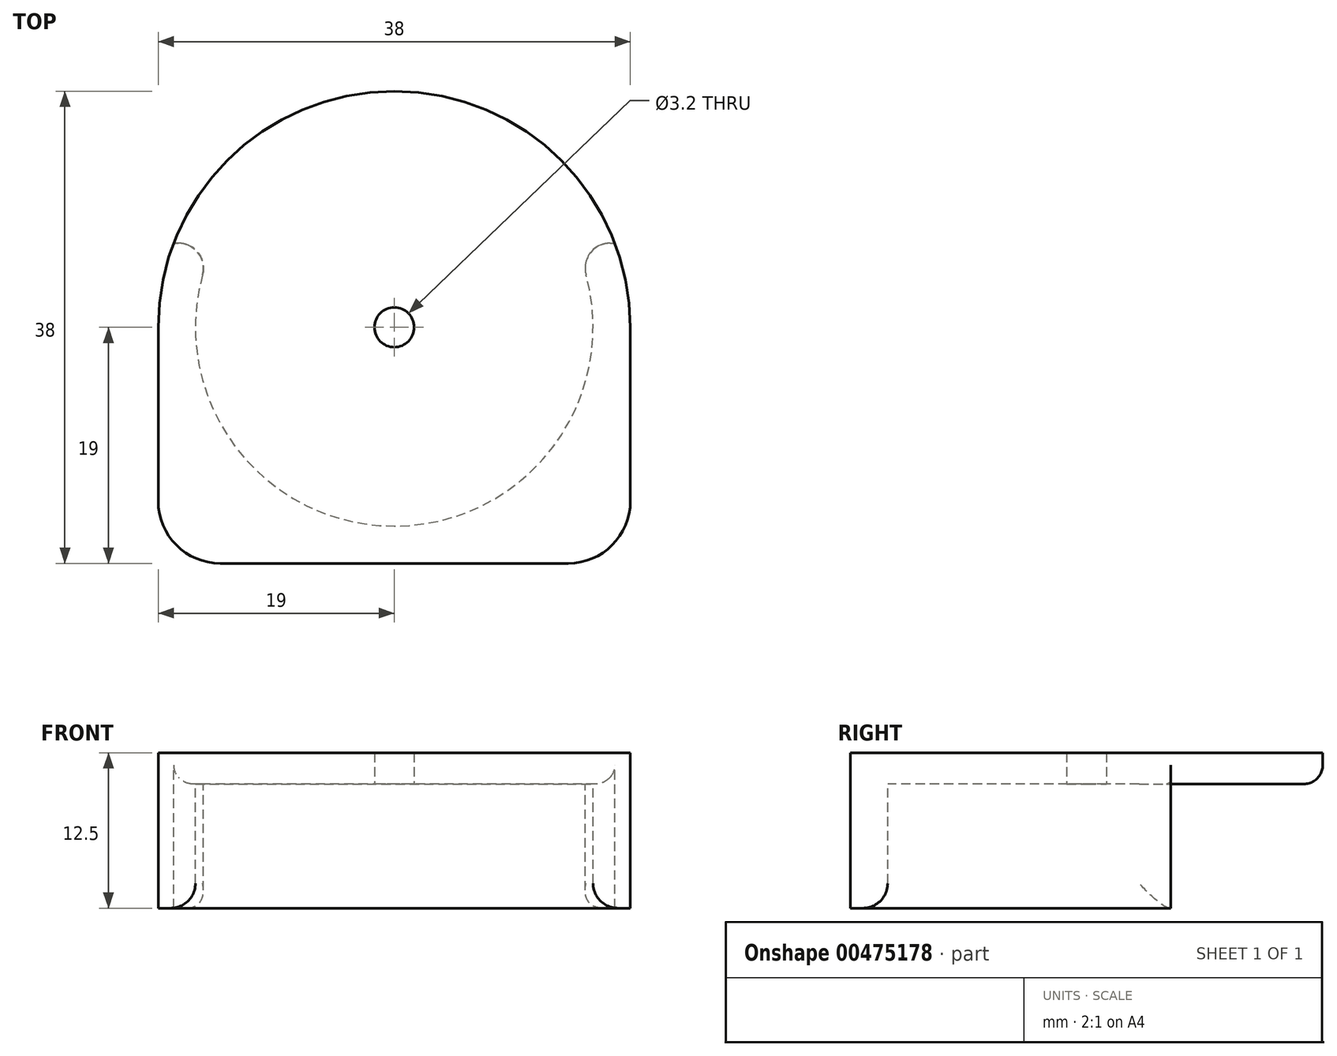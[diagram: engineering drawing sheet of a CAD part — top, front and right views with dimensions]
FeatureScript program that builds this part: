
annotation { "Feature Type Name" : "Feature", "Feature Type Description" : "" }
export const myFeature = defineFeature(function(context is Context, id is Id, definition is map)
    precondition{}
    {
        {
            var Q0;
            Q0=qCreatedBy(makeId("Top.planeOp"),FACE);
            var sketch = newSketch(context, id + "F0", { "sketchPlane" : qUnion([Q0])});
            skArc(sketch, "E0", {"start": v(-14.5, 6.76) * mm, "mid": v(0, -16) * mm, "end": v(14.5, 6.76) * mm});
            skCircle(sketch, "E1", {"center": v(0, 0) * mm, "radius": 19 * mm});
            skLineSegment(sketch, "E2", {"start": v(-14.5, 6.76) * mm, "end": v(14.5, 6.76) * mm});
            skLineSegment(sketch, "E3.bottom", {"start": v(14, -19) * mm, "end": v(-14, -19) * mm});
            skLineSegment(sketch, "E3.left", {"start": v(19, -14) * mm, "end": v(19, 0) * mm});
            skLineSegment(sketch, "E3.right", {"start": v(-19, -14) * mm, "end": v(-19, 0) * mm});
            skPoint(sketch, "E4.orphan", {"position": v(-19, 19) * mm});
            skPoint(sketch, "E5.orphan", {"position": v(19, 19) * mm});
            skPoint(sketch, "E6.visualSharp", {"position": v(-19, -19) * mm});
            skArc(sketch, "E6.filletArc", {"start": v(-19, -14) * mm, "mid": v(-17.54, -17.54) * mm, "end": v(-14, -19) * mm});
            skPoint(sketch, "E7.visualSharp", {"position": v(19, -19) * mm});
            skArc(sketch, "E7.filletArc", {"start": v(14, -19) * mm, "mid": v(17.54, -17.54) * mm, "end": v(19, -14) * mm});
            skLineSegment(sketch, "E8", {"start": v(-14.5, 6.76) * mm, "end": v(-17.76, 6.76) * mm});
            skLineSegment(sketch, "E9", {"start": v(14.5, 6.76) * mm, "end": v(17.76, 6.76) * mm});
            skSolve(sketch);
        }
        {
            var Q0;
            Q0 = qSketchRegion(id + "F0", true);
            var Q1;
            Q1=makeQuery(id+"F0.imprint","IMPRINT",FACE,{"disambiguationData":[TD([[makeQuery(id+"F0.imprint","IMPRINT",EDGE,{"derivedFrom":sQuery(id+"F0.wireOp",EDGE,"E0")}),1.0]])]});
            extrude(context, id + "F1", {"entities" : qUnion([Q0, Q1]), "depth" : 2.5 * mm, "offsetDistance" : 25 * mm});
        }
        {
            var Q0;
            Q0=makeQuery(id+"F0.imprint","IMPRINT",FACE,{"disambiguationData":[TD([[makeQuery(id+"F0.imprint","IMPRINT",EDGE,{"derivedFrom":sQuery(id+"F0.wireOp",EDGE,"E0")}),-1.0]])]});
            var Q1;
            {var subQ0=sQuery(id+"F0.wireOp",EDGE,"E3.left");Q1=makeQuery(id+"F0.imprint","IMPRINT",FACE,{"disambiguationData":[TD([[makeQuery(id+"F0.imprint","IMPRINT",EDGE,{"derivedFrom":subQ0}),1.0]])]});}
            var Q2;
            {var subQ0=sQuery(id+"F0.wireOp",EDGE,"E3.right");Q2=makeQuery(id+"F0.imprint","IMPRINT",FACE,{"disambiguationData":[TD([[makeQuery(id+"F0.imprint","IMPRINT",EDGE,{"derivedFrom":subQ0}),-1.0]])]});}
            extrude(context, id + "F2", {"entities" : qUnion([Q0, Q1, Q2]), "operationType" : NewBodyOperationType.ADD, "oppositeDirection" : true, "depth" : 10 * mm, "offsetDistance" : 25 * mm});
        }
        {
            var Q0;
            Q0=makeQuery(id+"F0.imprint","IMPRINT",FACE,{"disambiguationData":[TD([[makeQuery(id+"F0.imprint","IMPRINT",EDGE,{"derivedFrom":sQuery(id+"F0.wireOp",EDGE,"E0")}),1.0]])]});
            var sketch = newSketch(context, id + "F3", { "sketchPlane" : qUnion([Q0])});
            skCircle(sketch, "E10", {"center": v(0, 0) * mm, "radius": 1.6 * mm});
            skSolve(sketch);
        }
        {
            var Q0;
            Q0=makeQuery(id+"F3.imprint","IMPRINT",FACE,{"disambiguationData":[TD([[makeQuery(id+"F3.imprint","IMPRINT",EDGE,{"derivedFrom":sQuery(id+"F3.wireOp",EDGE,"E10")}),1.0]])]});
            extrude(context, id + "F4", {"entities" : qUnion([Q0]), "operationType" : NewBodyOperationType.REMOVE, "depth" : 25 * mm, "offsetDistance" : 25 * mm});
        }
        {
            var Q0;
            Q0=makeQuery(id+"F1.opExtrude","CAP_EDGE",EDGE,{"disambiguationData":[OSD([sQuery(id+"F0.wireOp",EDGE,"E1")])],"isStart":true});
            fillet(context, id + "F5", {"entities" : qUnion([Q0]), "radius" : 1.5 * mm, "tangentPropagation" : true, "allowEdgeOverflow" : false});
        }
        {
            var Q0;
            Q0=makeQuery(id+"F2.opExtrude","SWEPT_EDGE",EDGE,{"disambiguationData":[OSD([sQuery(id+"F0.wireOp",EDGE,"E0"),sQuery(id+"F0.wireOp",EDGE,"E2"),sQuery(id+"F0.wireOp",EDGE,"E9")])]});
            var Q1;
            Q1=makeQuery(id+"F2.opExtrude","SWEPT_EDGE",EDGE,{"disambiguationData":[OSD([sQuery(id+"F0.wireOp",EDGE,"E0"),sQuery(id+"F0.wireOp",EDGE,"E2"),sQuery(id+"F0.wireOp",EDGE,"E8")])]});
            var Q2;
            Q2=makeQuery(id+"F2.opExtrude","CAP_EDGE",EDGE,{"disambiguationData":[OSD([sQuery(id+"F0.wireOp",EDGE,"E0")])],"isStart":false});
            fillet(context, id + "F6", {"entities" : qUnion([Q0, Q1, Q2]), "radius" : 2 * mm, "tangentPropagation" : true, "allowEdgeOverflow" : false});
        }
    });
